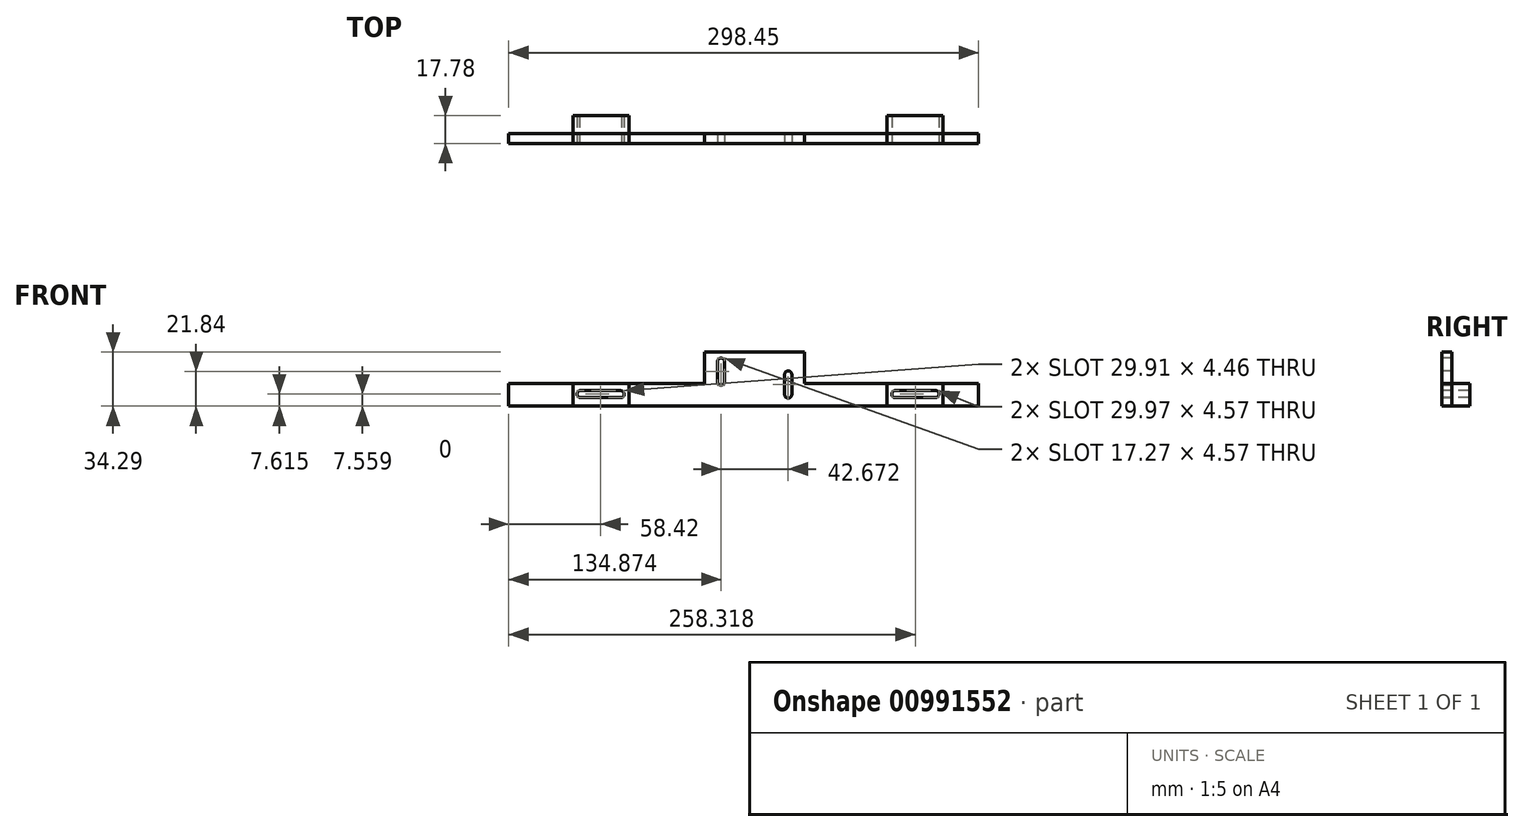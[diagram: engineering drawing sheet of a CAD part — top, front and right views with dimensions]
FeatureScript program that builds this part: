
annotation { "Feature Type Name" : "Feature", "Feature Type Description" : "" }
export const myFeature = defineFeature(function(context is Context, id is Id, definition is map)
    precondition{}
    {
        {
            var Q0;
            Q0=qCreatedBy(makeId("Front.planeOp"),FACE);
            var sketch = newSketch(context, id + "F0", { "sketchPlane" : qUnion([Q0])});
            skLineSegment(sketch, "E0.bottom", {"start": v(-144.1, 15.8) * mm, "end": v(-19.63, 15.8) * mm});
            skLineSegment(sketch, "E0.top", {"start": v(-144.1, 1.58) * mm, "end": v(154.36, 1.58) * mm});
            skLineSegment(sketch, "E0.left", {"start": v(-144.1, 15.8) * mm, "end": v(-144.1, 1.58) * mm});
            skLineSegment(sketch, "E0.right", {"start": v(154.36, 15.8) * mm, "end": v(154.36, 1.58) * mm});
            skLineSegment(sketch, "E1.top", {"start": v(-19.63, 35.87) * mm, "end": v(43.87, 35.87) * mm});
            skLineSegment(sketch, "E1.left", {"start": v(-19.63, 15.8) * mm, "end": v(-19.63, 35.87) * mm});
            skLineSegment(sketch, "E1.right", {"start": v(43.87, 15.8) * mm, "end": v(43.87, 35.87) * mm});
            skPoint(sketch, "E2.centerSnap0", {"position": v(-144.1, 8.69) * mm});
            skLineSegment(sketch, "E3.trimOffspring", {"start": v(43.87, 15.8) * mm, "end": v(154.36, 15.8) * mm});
            skArc(sketch, "E4", {"start": v(4066.66, 23.56) * mm, "mid": v(4068.97, 21.3) * mm, "end": v(4071.23, 23.61) * mm});
            skArc(sketch, "E5", {"start": v(4071.36, 10.91) * mm, "mid": v(4074.4, 8.78) * mm, "end": v(4075.45, 12.35) * mm});
            skLineSegment(sketch, "E6", {"start": v(4071.23, 23.61) * mm, "end": v(4071.36, 10.91) * mm});
            skLineSegment(sketch, "E7", {"start": v(4066.66, 23.56) * mm, "end": v(4075.45, 12.35) * mm});
            skArc(sketch, "E8", {"start": v(-99.08, 11.37) * mm, "mid": v(-100.63, 8.83) * mm, "end": v(-98.37, 6.9) * mm});
            skArc(sketch, "E9", {"start": v(-72.26, 6.9) * mm, "mid": v(-70.71, 9.44) * mm, "end": v(-72.97, 11.37) * mm});
            skLineSegment(sketch, "E10", {"start": v(-98.37, 6.9) * mm, "end": v(-72.26, 6.9) * mm});
            skLineSegment(sketch, "E11", {"start": v(-99.08, 11.37) * mm, "end": v(-72.97, 11.37) * mm});
            skArc(sketch, "E12", {"start": v(-6.93, 29.77) * mm, "mid": v(-9.22, 32.06) * mm, "end": v(-11.5, 29.77) * mm});
            skArc(sketch, "E13", {"start": v(-11.5, 17.07) * mm, "mid": v(-9.22, 14.78) * mm, "end": v(-6.93, 17.07) * mm});
            skLineSegment(sketch, "E14", {"start": v(-11.5, 17.07) * mm, "end": v(-11.5, 29.77) * mm});
            skLineSegment(sketch, "E15", {"start": v(-6.93, 17.07) * mm, "end": v(-6.93, 29.77) * mm});
            skArc(sketch, "E16", {"start": v(35.74, 21.64) * mm, "mid": v(33.46, 23.93) * mm, "end": v(31.17, 21.64) * mm});
            skArc(sketch, "E17", {"start": v(31.17, 8.94) * mm, "mid": v(33.46, 6.66) * mm, "end": v(35.74, 8.94) * mm});
            skLineSegment(sketch, "E18", {"start": v(35.74, 8.94) * mm, "end": v(35.74, 21.64) * mm});
            skLineSegment(sketch, "E19", {"start": v(31.17, 21.64) * mm, "end": v(31.17, 8.94) * mm});
            skArc(sketch, "E20", {"start": v(101.53, 11.48) * mm, "mid": v(99.24, 9.2) * mm, "end": v(101.53, 6.9) * mm});
            skArc(sketch, "E21", {"start": v(126.93, 6.9) * mm, "mid": v(129.21, 9.2) * mm, "end": v(126.93, 11.48) * mm});
            skLineSegment(sketch, "E22", {"start": v(101.53, 6.9) * mm, "end": v(126.93, 6.9) * mm});
            skLineSegment(sketch, "E23", {"start": v(101.53, 11.48) * mm, "end": v(126.93, 11.48) * mm});
            skLineSegment(sketch, "E24", {"start": v(-103.2, 15.8) * mm, "end": v(-103.2, 1.58) * mm});
            skLineSegment(sketch, "E25", {"start": v(-67.64, 15.8) * mm, "end": v(-67.64, 1.58) * mm});
            skLineSegment(sketch, "E26", {"start": v(96.2, 15.8) * mm, "end": v(96.2, 1.58) * mm});
            skLineSegment(sketch, "E27", {"start": v(131.75, 15.8) * mm, "end": v(131.75, 1.58) * mm});
            skSolve(sketch);
        }
        {
            var Q0;
            {var subQ0=sQuery(id+"F0.wireOp",EDGE,"E0.left");Q0=makeQuery(id+"F0.imprint","IMPRINT",FACE,{"disambiguationData":[TD([[makeQuery(id+"F0.imprint","IMPRINT",EDGE,{"derivedFrom":subQ0}),1.0]])]});}
            var Q1;
            Q1=makeQuery(id+"F0.imprint","IMPRINT",FACE,{"disambiguationData":[TD([[makeQuery(id+"F0.imprint","IMPRINT",EDGE,{"derivedFrom":sQuery(id+"F0.wireOp",EDGE,"E8")}),-1.0]])]});
            var Q2;
            Q2=makeQuery(id+"F0.imprint","IMPRINT",FACE,{"disambiguationData":[TD([[makeQuery(id+"F0.imprint","IMPRINT",EDGE,{"derivedFrom":sQuery(id+"F0.wireOp",EDGE,"E1.top")}),-1.0]])]});
            var Q3;
            Q3=makeQuery(id+"F0.imprint","IMPRINT",FACE,{"disambiguationData":[TD([[makeQuery(id+"F0.imprint","IMPRINT",EDGE,{"derivedFrom":sQuery(id+"F0.wireOp",EDGE,"E20")}),-1.0]])]});
            var Q4;
            {var subQ0=sQuery(id+"F0.wireOp",EDGE,"E0.right");Q4=makeQuery(id+"F0.imprint","IMPRINT",FACE,{"disambiguationData":[TD([[makeQuery(id+"F0.imprint","IMPRINT",EDGE,{"derivedFrom":subQ0}),-1.0]])]});}
            extrude(context, id + "F1", {"entities" : qUnion([Q0, Q1, Q2, Q3, Q4]), "oppositeDirection" : true, "depth" : 6.35 * mm, "offsetDistance" : 25.4 * mm});
        }
        {
            var Q0;
            Q0=makeQuery(id+"F0.imprint","IMPRINT",FACE,{"disambiguationData":[TD([[makeQuery(id+"F0.imprint","IMPRINT",EDGE,{"derivedFrom":sQuery(id+"F0.wireOp",EDGE,"E8")}),-1.0]])]});
            var Q1;
            Q1=makeQuery(id+"F0.imprint","IMPRINT",FACE,{"disambiguationData":[TD([[makeQuery(id+"F0.imprint","IMPRINT",EDGE,{"derivedFrom":sQuery(id+"F0.wireOp",EDGE,"E20")}),-1.0]])]});
            extrude(context, id + "F2", {"entities" : qUnion([Q0, Q1]), "oppositeDirection" : true, "depth" : 17.78 * mm, "offsetDistance" : 25.4 * mm});
        }
    });
